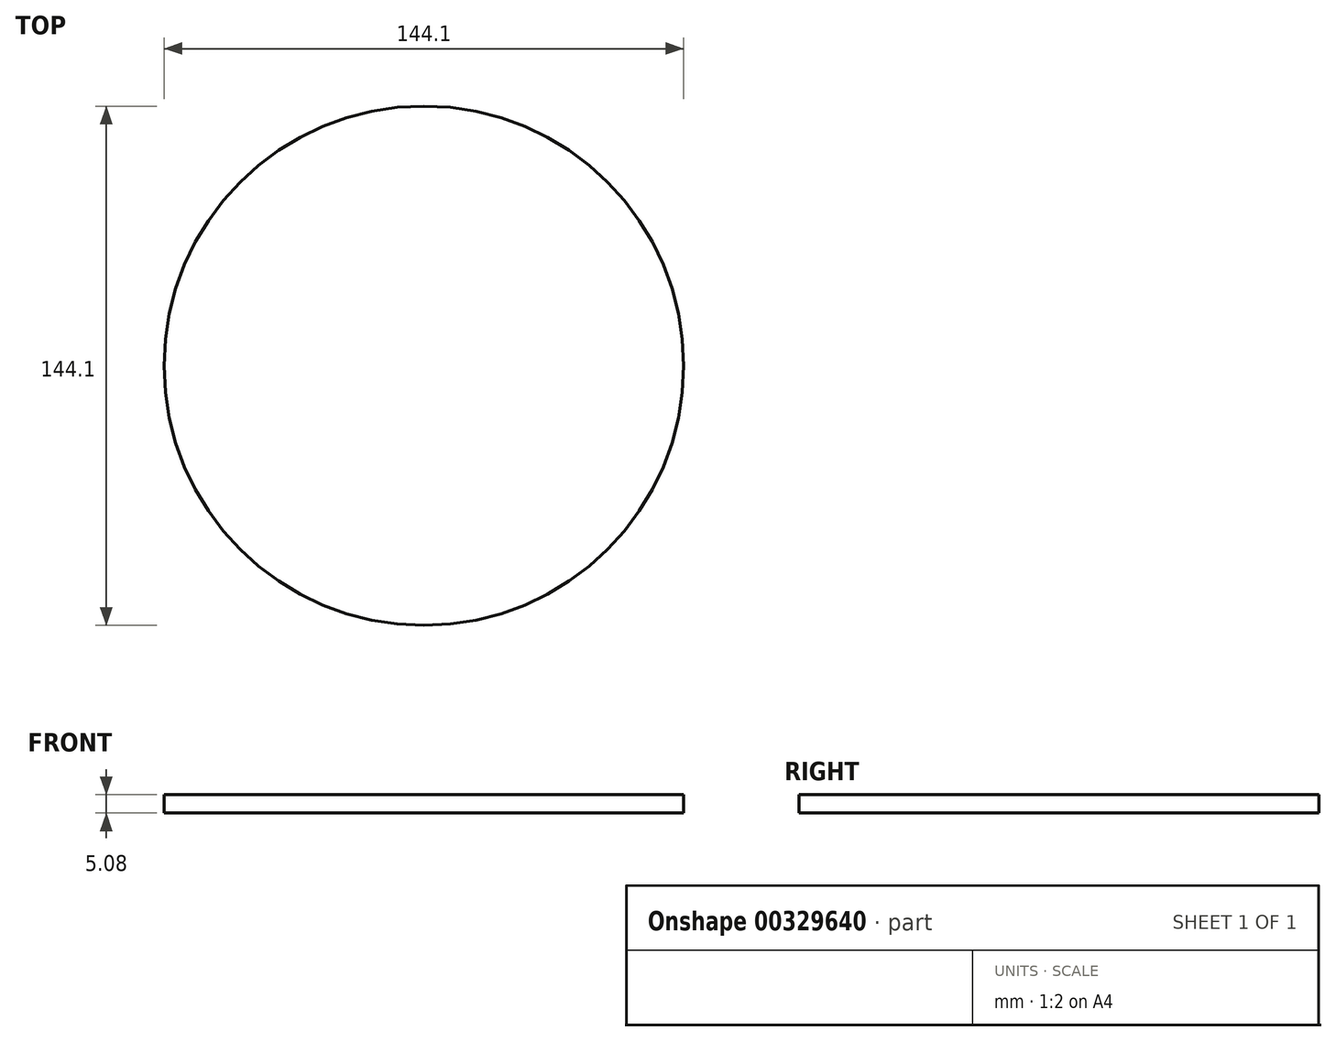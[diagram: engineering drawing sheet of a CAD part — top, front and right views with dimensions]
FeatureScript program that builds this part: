
annotation { "Feature Type Name" : "Feature", "Feature Type Description" : "" }
export const myFeature = defineFeature(function(context is Context, id is Id, definition is map)
    precondition{}
    {
        {
            var Q0;
            Q0=qCreatedBy(makeId("Top.planeOp"),FACE);
            var sketch = newSketch(context, id + "F0", { "sketchPlane" : qUnion([Q0])});
            skCircle(sketch, "E0", {"center": v(0, 0) * mm, "radius": 72.05 * mm});
            skSolve(sketch);
        }
        {
            var Q0;
            Q0 = qSketchRegion(id + "F0", true);
            extrude(context, id + "F1", {"entities" : qUnion([Q0]), "depth" : 5.08 * mm});
        }
    });
